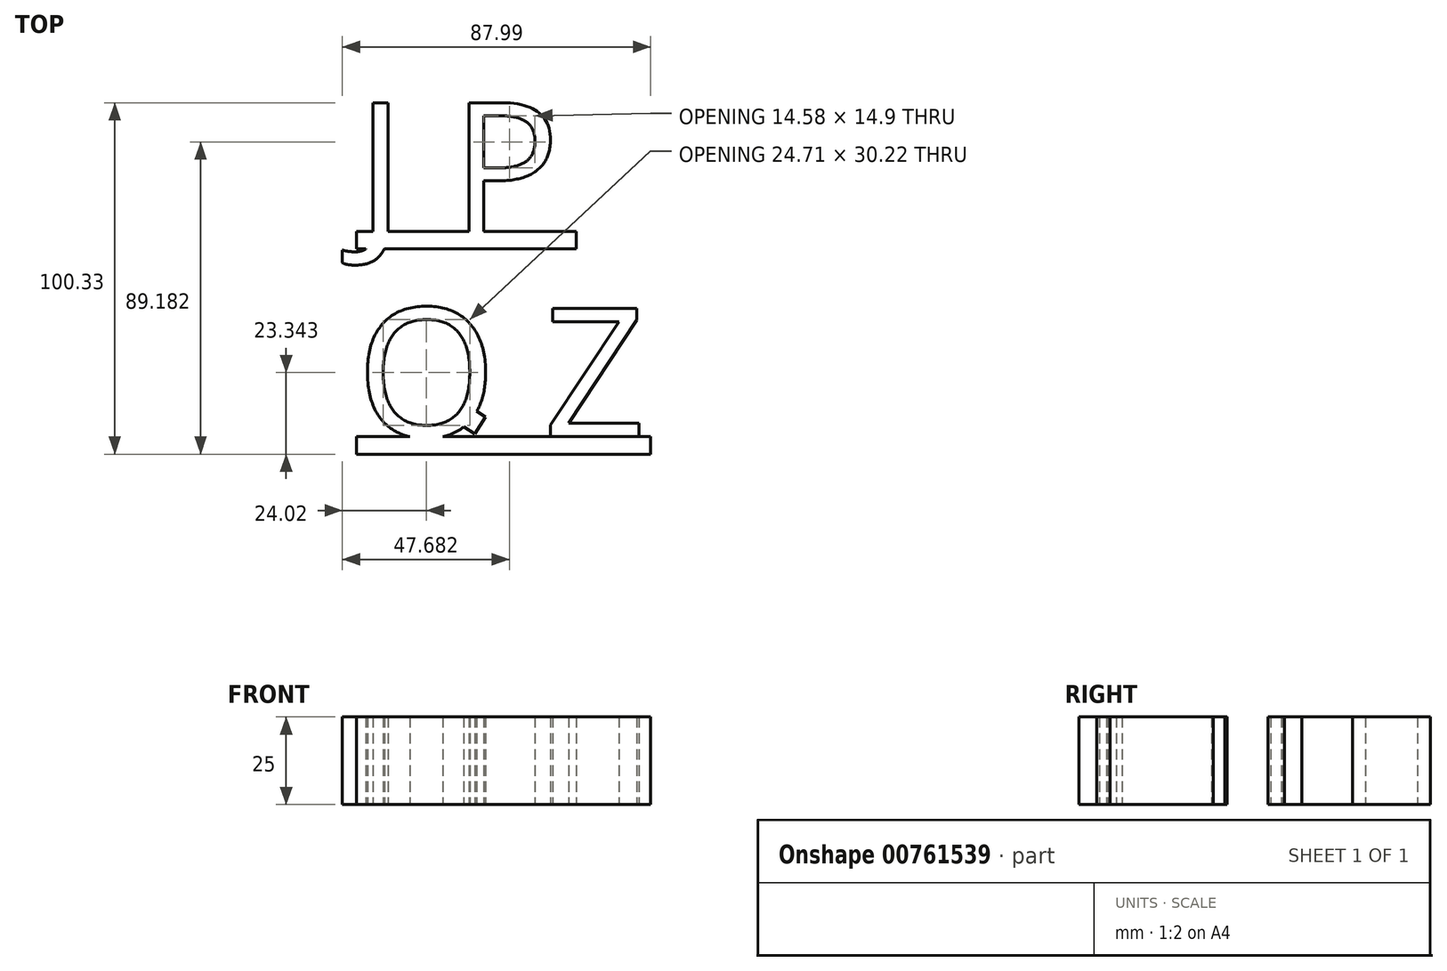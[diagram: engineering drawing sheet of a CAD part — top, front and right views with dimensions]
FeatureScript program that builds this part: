
annotation { "Feature Type Name" : "Feature", "Feature Type Description" : "" }
export const myFeature = defineFeature(function(context is Context, id is Id, definition is map)
    precondition{}
    {
        {
            var Q0;
            Q0=qCreatedBy(makeId("Top.planeOp"),FACE);
            var sketch = newSketch(context, id + "F0", { "sketchPlane" : qUnion([Q0])});
            skText(sketch, "E0", { "text": "J P", "fontName": "OpenSans-Regular.ttf"});
            skText(sketch, "E1", { "text": "O Z", "fontName": "OpenSans-Regular.ttf"});
            skPoint(sketch, "E1.firstSnap0", {"position": v(0, 18.5) * mm});
            skLineSegment(sketch, "E2.bottom", {"start": v(0, 0) * mm, "end": v(62.73, 0) * mm});
            skLineSegment(sketch, "E2.top", {"start": v(0, -5) * mm, "end": v(62.73, -5) * mm});
            skLineSegment(sketch, "E2.left", {"start": v(0, 0) * mm, "end": v(0, -5) * mm});
            skLineSegment(sketch, "E2.right", {"start": v(62.73, 0) * mm, "end": v(62.73, -5) * mm});
            skLineSegment(sketch, "E3.bottom", {"start": v(0, -58.64) * mm, "end": v(83.98, -58.64) * mm});
            skLineSegment(sketch, "E3.top", {"start": v(0, -63.64) * mm, "end": v(83.98, -63.64) * mm});
            skLineSegment(sketch, "E3.left", {"start": v(0, -58.64) * mm, "end": v(0, -63.64) * mm});
            skLineSegment(sketch, "E3.right", {"start": v(83.98, -58.64) * mm, "end": v(83.98, -63.64) * mm});
            skLineSegment(sketch, "E4", {"start": v(30.53, -55.78) * mm, "end": v(33.76, -57.82) * mm});
            skLineSegment(sketch, "E5", {"start": v(33.76, -57.82) * mm, "end": v(36.83, -52.95) * mm});
            skLineSegment(sketch, "E6", {"start": v(36.83, -52.95) * mm, "end": v(33.76, -51.02) * mm});
            skLineSegment(sketch, "E7", {"start": v(30.53, -55.78) * mm, "end": v(33.76, -51.02) * mm});
            const initialGuessF0  = {"E0": [0, 0, 1, 0, 0.037], "E1": [0, -0.05864, 1, 0, 0.037]};
            skSetInitialGuess(sketch, initialGuessF0);
            skSolve(sketch);
        }
        {
            var Q0;
            Q0 = qSketchRegion(id + "F0", true);
            extrude(context, id + "F1", {"entities" : qUnion([Q0]), "depth" : 25 * mm, "offsetDistance" : 25 * mm});
        }
    });
